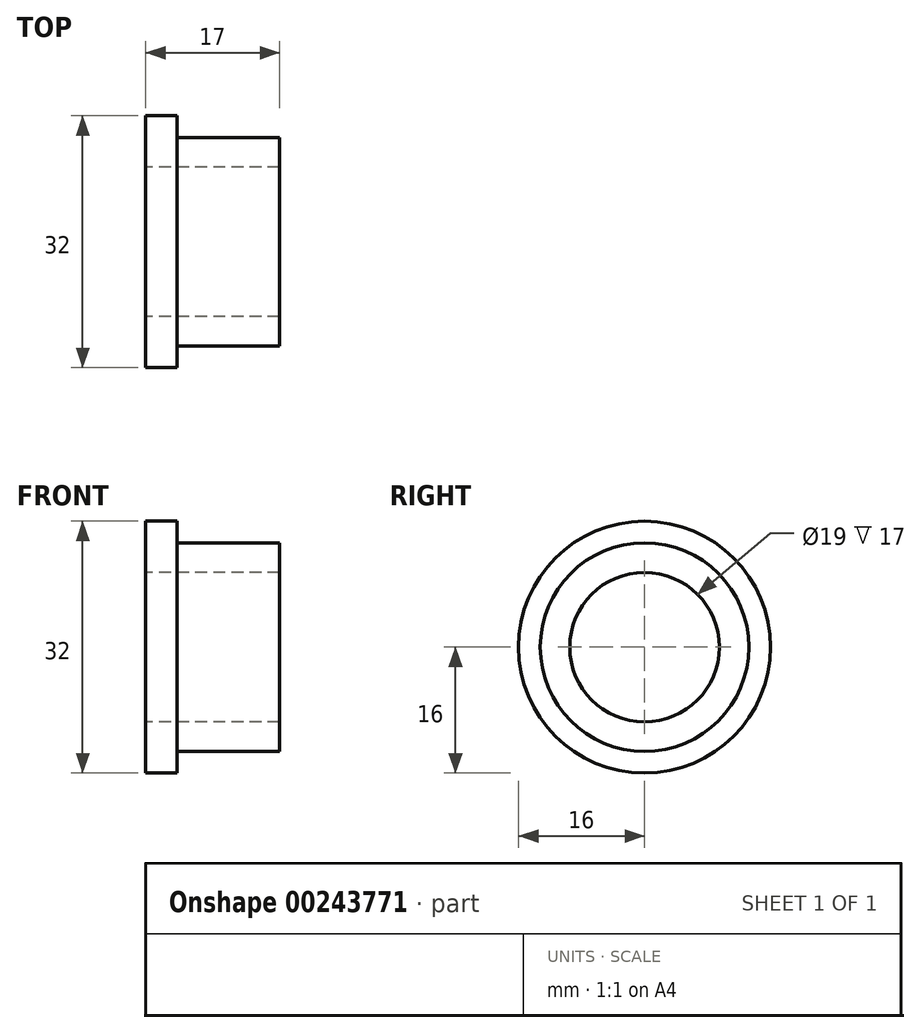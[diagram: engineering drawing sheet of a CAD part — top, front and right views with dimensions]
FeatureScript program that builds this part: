
annotation { "Feature Type Name" : "Feature", "Feature Type Description" : "" }
export const myFeature = defineFeature(function(context is Context, id is Id, definition is map)
    precondition{}
    {
        {
            var Q0;
            Q0=qCreatedBy(makeId("Front.planeOp"),FACE);
            var sketch = newSketch(context, id + "F0", { "sketchPlane" : qUnion([Q0])});
            skLineSegment(sketch, "E0", {"start": v(0, 9.5) * mm, "end": v(0, 16) * mm});
            skLineSegment(sketch, "E1", {"start": v(0, 16) * mm, "end": v(4, 16) * mm});
            skLineSegment(sketch, "E2", {"start": v(4, 16) * mm, "end": v(4, 13.25) * mm});
            skLineSegment(sketch, "E3", {"start": v(4, 13.25) * mm, "end": v(17, 13.25) * mm});
            skLineSegment(sketch, "E4", {"start": v(17, 13.25) * mm, "end": v(17, 9.5) * mm});
            skLineSegment(sketch, "E5", {"start": v(17, 9.5) * mm, "end": v(0, 9.5) * mm});
            skLineSegment(sketch, "E6", {"start": v(-7.64, 0) * mm, "end": v(20.03, 0) * mm, "construction": true});
            skSolve(sketch);
        }
        {
            var Q0;
            Q0=makeQuery(id+"F0.imprint","IMPRINT",FACE,{"disambiguationData":[TD([[makeQuery(id+"F0.imprint","IMPRINT",EDGE,{"derivedFrom":sQuery(id+"F0.wireOp",EDGE,"E0")}),-1.0]])]});
            var Q1;
            Q1=sQuery(id+"F0.wireOp",EDGE,"E6");
            revolve(context, id + "F1", {"entities" : qUnion([Q0]), "axis" : qUnion([Q1]), "revolveType" : RevolveType.FULL});
        }
    });
